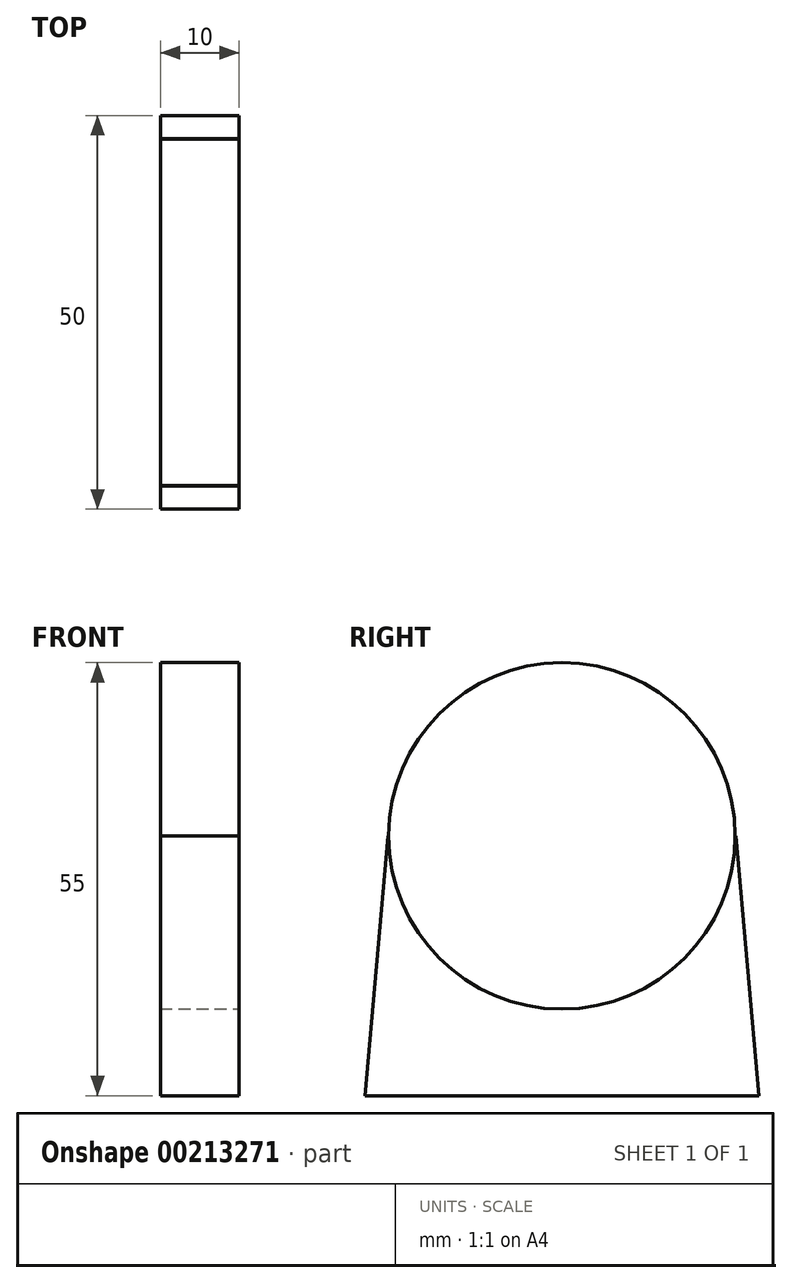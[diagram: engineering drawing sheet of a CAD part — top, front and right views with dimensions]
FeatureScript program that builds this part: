
annotation { "Feature Type Name" : "Feature", "Feature Type Description" : "" }
export const myFeature = defineFeature(function(context is Context, id is Id, definition is map)
    precondition{}
    {
        {
            var Q0;
            Q0=qCreatedBy(makeId("Right.planeOp"),FACE);
            var sketch = newSketch(context, id + "F0", { "sketchPlane" : qUnion([Q0])});
            skCircle(sketch, "E0", {"center": v(0, 0) * mm, "radius": 22 * mm});
            skLineSegment(sketch, "E1", {"start": v(25, -33) * mm, "end": v(0, -33) * mm});
            skLineSegment(sketch, "E2", {"start": v(0, -33) * mm, "end": v(-25, -33) * mm});
            skLineSegment(sketch, "E3", {"start": v(-25, -33) * mm, "end": v(-22.09, 0) * mm});
            skLineSegment(sketch, "E4", {"start": v(25, -33) * mm, "end": v(22.09, 0) * mm});
            skSolve(sketch);
        }
        {
            var Q0;
            Q0=sQuery(id+"F0.wireOp",EDGE,"E3");
            var Q1;
            Q1=sQuery(id+"F0.wireOp",EDGE,"E1");
            var Q2;
            Q2=sQuery(id+"F0.wireOp",EDGE,"E0");
            var Q3;
            Q3=sQuery(id+"F0.wireOp",EDGE,"E4");
            var Q4;
            Q4=sQuery(id+"F0.wireOp",EDGE,"E2");
            extrude(context, id + "F1", {"bodyType" : ToolBodyType.SURFACE, "surfaceEntities" : qUnion([Q0, Q1, Q2, Q3, Q4]), "depth" : 10 * mm});
        }
    });
